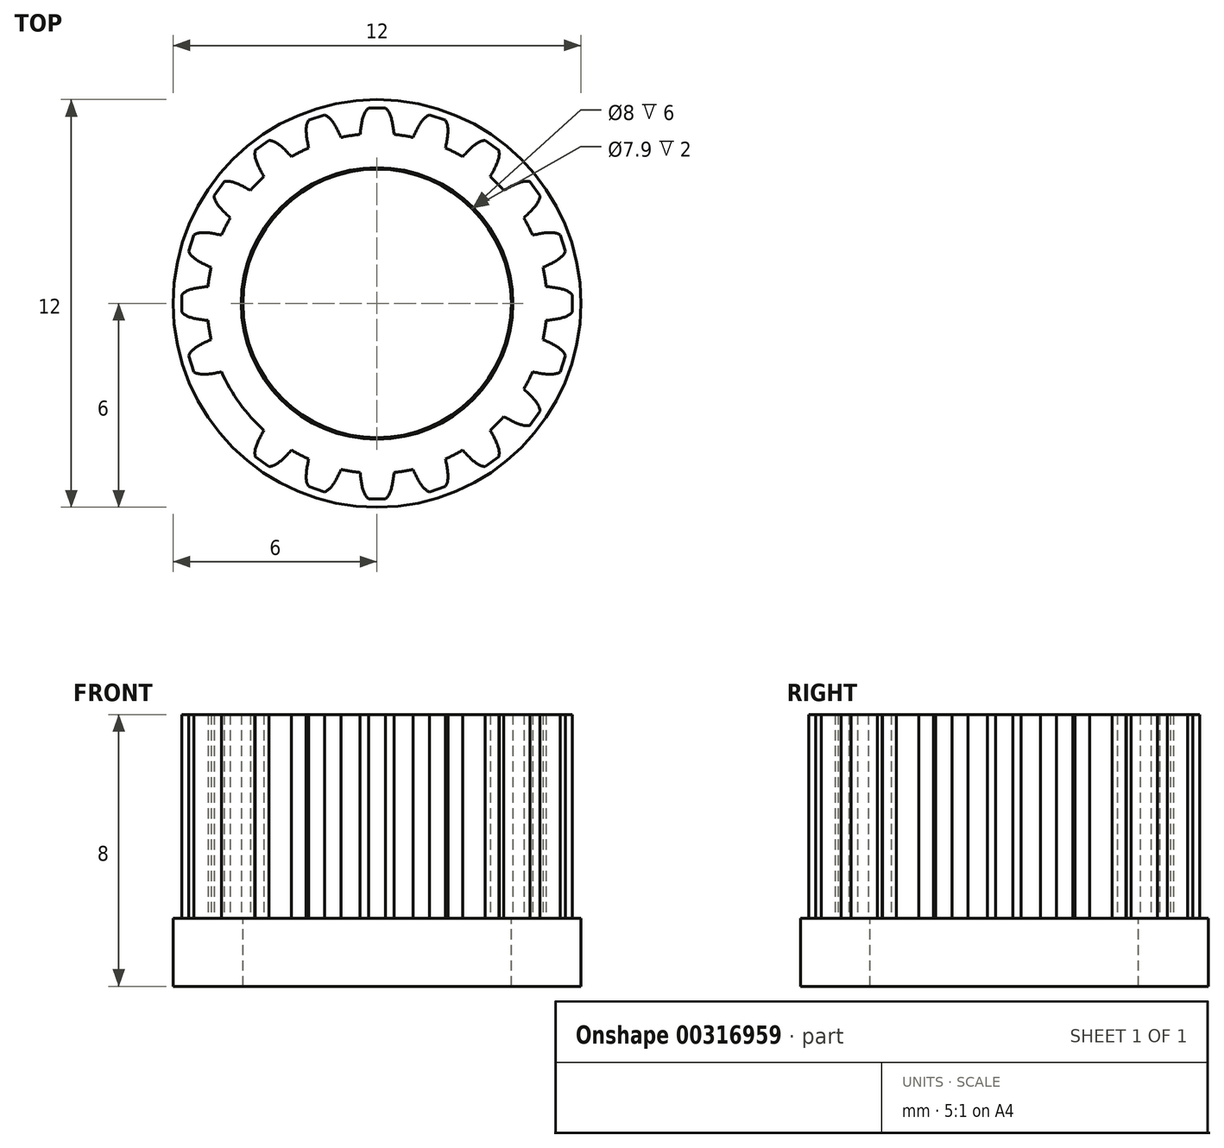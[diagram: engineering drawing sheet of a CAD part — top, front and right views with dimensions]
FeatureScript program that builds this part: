
annotation { "Feature Type Name" : "Feature", "Feature Type Description" : "" }
export const myFeature = defineFeature(function(context is Context, id is Id, definition is map)
    precondition{}
    {
        {
            var Q0;
            Q0=qCreatedBy(makeId("Top.planeOp"),FACE);
            var sketch = newSketch(context, id + "F0", { "sketchPlane" : qUnion([Q0])});
            skArc(sketch, "E0", {"start": v(-4, 0) * mm, "mid": v(-2.83, -2.83) * mm, "end": v(0, -4) * mm});
            skArc(sketch, "E1", {"start": v(0.5, -4.97) * mm, "mid": v(0, 5) * mm, "end": v(-0.5, -4.97) * mm});
            skPoint(sketch, "E2", {"position": v(0, -5) * mm});
            skPoint(sketch, "E3", {"position": v(-0.5, -4.97) * mm});
            skPoint(sketch, "E4", {"position": v(0.5, -4.97) * mm});
            skPoint(sketch, "E5.start.orphan", {"position": v(0, -5.75) * mm});
            skArc(sketch, "E6.1.0", {"start": v(2.01, -4.58) * mm, "mid": v(-1.55, 4.76) * mm, "end": v(1.06, -4.89) * mm});
            skArc(sketch, "E6.2.0", {"start": v(3.33, -3.73) * mm, "mid": v(-2.94, 4.05) * mm, "end": v(2.52, -4.32) * mm});
            skArc(sketch, "E6.3.0", {"start": v(4.32, -2.52) * mm, "mid": v(-4.05, 2.94) * mm, "end": v(3.73, -3.33) * mm});
            skArc(sketch, "E6.4.0", {"start": v(4.89, -1.06) * mm, "mid": v(-4.76, 1.55) * mm, "end": v(4.58, -2.01) * mm});
            skArc(sketch, "E6.5.0", {"start": v(4.97, 0.5) * mm, "mid": v(-5, 0) * mm, "end": v(4.97, -0.5) * mm});
            skArc(sketch, "E6.6.0", {"start": v(4.58, 2.01) * mm, "mid": v(-4.76, -1.55) * mm, "end": v(4.89, 1.06) * mm});
            skArc(sketch, "E6.7.0", {"start": v(3.73, 3.33) * mm, "mid": v(0.78, 4.94) * mm, "end": v(-2.52, 4.32) * mm});
            skArc(sketch, "E6.8.0", {"start": v(2.52, 4.32) * mm, "mid": v(-1.78, 4.67) * mm, "end": v(-4.76, 1.55) * mm});
            skArc(sketch, "E6.9.0", {"start": v(1.06, 4.89) * mm, "mid": v(-0.78, 4.94) * mm, "end": v(-2.52, 4.32) * mm});
            skArc(sketch, "E6.10.0", {"start": v(-0.5, 4.97) * mm, "mid": v(0, -5) * mm, "end": v(0.5, 4.97) * mm});
            skArc(sketch, "E6.11.0", {"start": v(-2.01, 4.58) * mm, "mid": v(-2.5, 4.34) * mm, "end": v(-2.94, 4.05) * mm});
            skArc(sketch, "E6.12.0", {"start": v(-3.33, 3.73) * mm, "mid": v(2.94, -4.05) * mm, "end": v(-2.52, 4.32) * mm});
            skArc(sketch, "E6.13.0", {"start": v(-4.32, 2.52) * mm, "mid": v(3.87, -3.16) * mm, "end": v(-3.33, 3.73) * mm});
            skArc(sketch, "E6.14.0", {"start": v(-4.89, 1.06) * mm, "mid": v(4.76, -1.55) * mm, "end": v(-4.58, 2.01) * mm});
            skArc(sketch, "E6.15.0", {"start": v(-4.97, -0.5) * mm, "mid": v(5, 0) * mm, "end": v(-4.97, 0.5) * mm});
            skArc(sketch, "E6.16.0", {"start": v(-4.58, -2.01) * mm, "mid": v(-2.04, -4.56) * mm, "end": v(1.55, -4.76) * mm});
            skArc(sketch, "E6.17.0", {"start": v(-3.73, -3.33) * mm, "mid": v(4.94, -0.78) * mm, "end": v(-2.52, 4.32) * mm});
            skArc(sketch, "E6.18.0", {"start": v(-2.52, -4.32) * mm, "mid": v(-1.3, -4.83) * mm, "end": v(0, -5) * mm});
            skArc(sketch, "E6.19.0", {"start": v(-1.06, -4.89) * mm, "mid": v(0, -5) * mm, "end": v(1.06, -4.89) * mm});
            skLineSegment(sketch, "E7", {"start": v(-1.78, -5.47) * mm, "end": v(-1.54, -5.55) * mm});
            skLineSegment(sketch, "E8", {"start": v(-1.78, -5.47) * mm, "end": v(-2.01, -5.4) * mm});
            skFitSpline(sketch, "E9", {"points": [v(-2.01, -4.58) * mm, v(-2.01, -5.4) * mm, v(-1.54, -5.55) * mm, v(-1.06, -4.89) * mm], "startDerivative": vector(-0.53, -2.62) * mm, "endDerivative": vector(1.11, 2.43) * mm});
            skLineSegment(sketch, "E10", {"start": v(0, -5.75) * mm, "end": v(-0.25, -5.75) * mm});
            skFitSpline(sketch, "E11", {"points": [v(-0.5, -4.97) * mm, v(-0.25, -5.75) * mm, v(0.25, -5.75) * mm, v(0.5, -4.97) * mm], "startDerivative": vector(0.3, -2.65) * mm, "endDerivative": vector(0.3, 2.65) * mm});
            skLineSegment(sketch, "E12", {"start": v(-3.38, -4.65) * mm, "end": v(-3.18, -4.8) * mm});
            skLineSegment(sketch, "E13", {"start": v(-3.38, -4.65) * mm, "end": v(-3.58, -4.5) * mm});
            skFitSpline(sketch, "E14", {"points": [v(-3.33, -3.73) * mm, v(-3.58, -4.5) * mm, v(-3.18, -4.8) * mm, v(-2.52, -4.32) * mm], "startDerivative": vector(-1.31, -2.33) * mm, "endDerivative": vector(1.8, 1.97) * mm});
            skPoint(sketch, "E15.orphan", {"position": v(-2.94, -4.05) * mm});
            skLineSegment(sketch, "E16", {"start": v(-4.65, -3.38) * mm, "end": v(-4.5, -3.58) * mm});
            skLineSegment(sketch, "E17", {"start": v(-4.5, -3.58) * mm, "end": v(-4.65, -3.38) * mm});
            skLineSegment(sketch, "E18", {"start": v(-4.65, -3.38) * mm, "end": v(-4.8, -3.18) * mm});
            skFitSpline(sketch, "E19", {"points": [v(-4.32, -2.52) * mm, v(-4.8, -3.18) * mm, v(-4.5, -3.58) * mm, v(-3.73, -3.33) * mm], "startDerivative": vector(-1.97, -1.8) * mm, "endDerivative": vector(2.33, 1.31) * mm});
            skPoint(sketch, "E20.orphan", {"position": v(-4.05, -2.94) * mm});
            skLineSegment(sketch, "E21", {"start": v(-5.47, -1.78) * mm, "end": v(-5.4, -2.01) * mm});
            skLineSegment(sketch, "E22", {"start": v(-5.47, -1.78) * mm, "end": v(-5.55, -1.54) * mm});
            skFitSpline(sketch, "E23", {"points": [v(-4.89, -1.06) * mm, v(-5.55, -1.54) * mm, v(-5.4, -2.01) * mm, v(-4.58, -2.01) * mm], "startDerivative": vector(-2.43, -1.11) * mm, "endDerivative": vector(2.62, 0.53) * mm});
            skPoint(sketch, "E24.orphan", {"position": v(-4.76, -1.55) * mm});
            skLineSegment(sketch, "E25", {"start": v(-5.75, 0) * mm, "end": v(-5.75, -0.25) * mm});
            skFitSpline(sketch, "E26.trimOffspring", {"points": [v(-4.97, 0.5) * mm, v(-5.75, 0.25) * mm, v(-5.75, -0.25) * mm, v(-4.97, -0.5) * mm], "startDerivative": vector(-2.65, -0.3) * mm, "endDerivative": vector(2.65, -0.3) * mm});
            skPoint(sketch, "E27.orphan", {"position": v(-5, 0) * mm});
            skArc(sketch, "E28.trimOffspring", {"start": v(-5, 0) * mm, "mid": v(-4.19, -2.73) * mm, "end": v(-2.01, -4.58) * mm});
            skArc(sketch, "E29.trimOffspring", {"start": v(-5, 0) * mm, "mid": v(-4.56, -2.04) * mm, "end": v(-3.33, -3.73) * mm});
            skPoint(sketch, "E30.start.orphan", {"position": v(-4.76, 1.55) * mm});
            skPoint(sketch, "E31.start.orphan", {"position": v(-2.94, 4.05) * mm});
            skArc(sketch, "E32.trimOffspring", {"start": v(-2.94, 4.05) * mm, "mid": v(-4.9, 1.03) * mm, "end": v(-4.32, -2.52) * mm});
            skArc(sketch, "E33.trimOffspring", {"start": v(-3.33, 3.73) * mm, "mid": v(-4.46, 2.27) * mm, "end": v(-4.97, 0.5) * mm});
            skPoint(sketch, "E34.orphan", {"position": v(-3.73, 3.33) * mm});
            skPoint(sketch, "E35.start.orphan", {"position": v(-4.05, 2.94) * mm});
            skPoint(sketch, "E36.start.orphan", {"position": v(-1.55, 4.76) * mm});
            skPoint(sketch, "E37.start.orphan", {"position": v(0, 5) * mm});
            skPoint(sketch, "E38.start.orphan", {"position": v(2.94, -4.05) * mm});
            skPoint(sketch, "E39.start.orphan", {"position": v(1.55, -4.76) * mm});
            skArc(sketch, "E40.trimOffspring", {"start": v(0.5, -4.97) * mm, "mid": v(4.76, -1.55) * mm, "end": v(3.33, 3.73) * mm});
            skArc(sketch, "E41.trimOffspring", {"start": v(1.55, -4.76) * mm, "mid": v(2.27, -4.46) * mm, "end": v(2.94, -4.05) * mm});
            skArc(sketch, "E42.trimOffspring", {"start": v(2.01, -4.58) * mm, "mid": v(2.7, -4.2) * mm, "end": v(3.33, -3.73) * mm});
            skArc(sketch, "E43.trimOffspring", {"start": v(3.33, -3.73) * mm, "mid": v(4.94, -0.78) * mm, "end": v(4.32, 2.52) * mm});
            skArc(sketch, "E44.trimOffspring", {"start": v(3.33, -3.73) * mm, "mid": v(3.54, -3.54) * mm, "end": v(3.73, -3.33) * mm});
            skArc(sketch, "E45.trimOffspring", {"start": v(3.73, -3.33) * mm, "mid": v(3.87, 3.16) * mm, "end": v(-2.52, 4.32) * mm});
            skArc(sketch, "E46.trimOffspring", {"start": v(4.32, -2.52) * mm, "mid": v(4.94, 0.78) * mm, "end": v(3.33, 3.73) * mm});
            skPoint(sketch, "E47.start.orphan", {"position": v(4.76, -1.55) * mm});
            skPoint(sketch, "E48.start.orphan", {"position": v(5, 0) * mm});
            skArc(sketch, "E49.trimOffspring", {"start": v(2.52, 4.32) * mm, "mid": v(-0.25, 5) * mm, "end": v(-2.94, 4.05) * mm});
            skArc(sketch, "E50.trimOffspring", {"start": v(2.52, 4.32) * mm, "mid": v(-1.55, 4.76) * mm, "end": v(-4.58, 2.01) * mm});
            skArc(sketch, "E51.trimOffspring", {"start": v(3.73, 3.33) * mm, "mid": v(3.54, 3.54) * mm, "end": v(3.33, 3.73) * mm});
            skArc(sketch, "E52.trimOffspring", {"start": v(-4.76, 1.55) * mm, "mid": v(-4.83, 1.3) * mm, "end": v(-4.89, 1.06) * mm});
            skArc(sketch, "E53.trimOffspring", {"start": v(-4.89, 1.06) * mm, "mid": v(-2.73, -4.19) * mm, "end": v(2.94, -4.05) * mm});
            skFitSpline(sketch, "E54.MirrorCS", {"points": [v(-4.97, -0.5) * mm, v(-5.75, -0.25) * mm, v(-5.75, 0.25) * mm, v(-4.97, 0.5) * mm], "startDerivative": vector(-2.65, 0.3) * mm, "endDerivative": vector(2.65, 0.3) * mm});
            skFitSpline(sketch, "E55.MirrorCS", {"points": [v(-4.89, 1.06) * mm, v(-5.55, 1.54) * mm, v(-5.4, 2.01) * mm, v(-4.58, 2.01) * mm], "startDerivative": vector(-2.43, 1.11) * mm, "endDerivative": vector(2.62, -0.53) * mm});
            skLineSegment(sketch, "E56.MirrorCS", {"start": v(-5.47, 1.78) * mm, "end": v(-5.4, 2.01) * mm});
            skLineSegment(sketch, "E57.MirrorCS", {"start": v(-5.47, 1.78) * mm, "end": v(-5.55, 1.54) * mm});
            skLineSegment(sketch, "E58.MirrorCS", {"start": v(-5.75, 0) * mm, "end": v(-5.75, 0.25) * mm});
            skFitSpline(sketch, "E59.MirrorCS", {"points": [v(-4.32, 2.52) * mm, v(-4.8, 3.18) * mm, v(-4.5, 3.58) * mm, v(-3.73, 3.33) * mm], "startDerivative": vector(-1.97, 1.8) * mm, "endDerivative": vector(2.33, -1.31) * mm});
            skLineSegment(sketch, "E60.MirrorCS", {"start": v(-4.5, 3.58) * mm, "end": v(-4.65, 3.38) * mm});
            skLineSegment(sketch, "E61.MirrorCS", {"start": v(-4.65, 3.38) * mm, "end": v(-4.8, 3.18) * mm});
            skFitSpline(sketch, "E62.MirrorCS", {"points": [v(-4.32, 2.52) * mm, v(-4.8, 3.18) * mm, v(-4.5, 3.58) * mm, v(-3.73, 3.33) * mm], "startDerivative": vector(-1.97, 1.8) * mm, "endDerivative": vector(2.33, -1.31) * mm});
            skFitSpline(sketch, "E63.MirrorCS", {"points": [v(-3.33, 3.73) * mm, v(-3.58, 4.5) * mm, v(-3.18, 4.8) * mm, v(-2.52, 4.32) * mm], "startDerivative": vector(-1.31, 2.33) * mm, "endDerivative": vector(1.8, -1.97) * mm});
            skLineSegment(sketch, "E64.MirrorCS", {"start": v(-3.38, 4.65) * mm, "end": v(-3.58, 4.5) * mm});
            skLineSegment(sketch, "E65.MirrorCS", {"start": v(-3.38, 4.65) * mm, "end": v(-3.18, 4.8) * mm});
            skFitSpline(sketch, "E66.MirrorCS", {"points": [v(-3.33, 3.73) * mm, v(-3.58, 4.5) * mm, v(-3.18, 4.8) * mm, v(-2.52, 4.32) * mm], "startDerivative": vector(-1.31, 2.33) * mm, "endDerivative": vector(1.8, -1.97) * mm});
            skArc(sketch, "E67.MirrorCS", {"start": v(-4, 0) * mm, "mid": v(-2.83, 2.83) * mm, "end": v(0, 4) * mm});
            skLineSegment(sketch, "E68.MirrorCS", {"start": v(0, 5.75) * mm, "end": v(-0.25, 5.75) * mm});
            skFitSpline(sketch, "E69.MirrorCS", {"points": [v(-0.5, 4.97) * mm, v(-0.25, 5.75) * mm, v(0.25, 5.75) * mm, v(0.5, 4.97) * mm], "startDerivative": vector(0.3, 2.65) * mm, "endDerivative": vector(0.3, -2.65) * mm});
            skFitSpline(sketch, "E70.MirrorCS", {"points": [v(-2.01, 4.58) * mm, v(-2.01, 5.4) * mm, v(-1.54, 5.55) * mm, v(-1.06, 4.89) * mm], "startDerivative": vector(-0.53, 2.62) * mm, "endDerivative": vector(1.11, -2.43) * mm});
            skLineSegment(sketch, "E71.MirrorCS", {"start": v(-1.78, 5.47) * mm, "end": v(-1.54, 5.55) * mm});
            skLineSegment(sketch, "E72.MirrorCS", {"start": v(-1.78, 5.47) * mm, "end": v(-2.01, 5.4) * mm});
            skArc(sketch, "E73.trimOffspring", {"start": v(-2.94, 4.05) * mm, "mid": v(0.53, -4.97) * mm, "end": v(2.01, 4.58) * mm});
            skArc(sketch, "E74.trimOffspring", {"start": v(-3.33, 3.73) * mm, "mid": v(2.27, -4.46) * mm, "end": v(-1.06, 4.89) * mm});
            skArc(sketch, "E75.trimOffspring", {"start": v(-2.94, 4.05) * mm, "mid": v(-1.03, -4.9) * mm, "end": v(4.32, 2.52) * mm});
            skArc(sketch, "E76.trimOffspring", {"start": v(-2.94, 4.05) * mm, "mid": v(-4.67, 1.78) * mm, "end": v(-4.89, -1.06) * mm});
            skArc(sketch, "E77.MirrorCS", {"start": v(4, 0) * mm, "mid": v(2.83, 2.83) * mm, "end": v(0, 4) * mm});
            skFitSpline(sketch, "E78.MirrorCS", {"points": [v(0.5, 4.97) * mm, v(0.25, 5.75) * mm, v(-0.25, 5.75) * mm, v(-0.5, 4.97) * mm], "startDerivative": vector(-0.3, 2.65) * mm, "endDerivative": vector(-0.3, -2.65) * mm});
            skLineSegment(sketch, "E79.MirrorCS", {"start": v(0, 5.75) * mm, "end": v(0.25, 5.75) * mm});
            skFitSpline(sketch, "E80.MirrorCS", {"points": [v(2.01, 4.58) * mm, v(2.01, 5.4) * mm, v(1.54, 5.55) * mm, v(1.06, 4.89) * mm], "startDerivative": vector(0.53, 2.62) * mm, "endDerivative": vector(-1.11, -2.43) * mm});
            skLineSegment(sketch, "E81.MirrorCS", {"start": v(1.78, 5.47) * mm, "end": v(2.01, 5.4) * mm});
            skLineSegment(sketch, "E82.MirrorCS", {"start": v(1.78, 5.47) * mm, "end": v(1.54, 5.55) * mm});
            skFitSpline(sketch, "E83.MirrorCS", {"points": [v(3.33, 3.73) * mm, v(3.58, 4.5) * mm, v(3.18, 4.8) * mm, v(2.52, 4.32) * mm], "startDerivative": vector(1.31, 2.33) * mm, "endDerivative": vector(-1.8, -1.97) * mm});
            skLineSegment(sketch, "E84.MirrorCS", {"start": v(3.38, 4.65) * mm, "end": v(3.18, 4.8) * mm});
            skLineSegment(sketch, "E85.MirrorCS", {"start": v(3.38, 4.65) * mm, "end": v(3.58, 4.5) * mm});
            skFitSpline(sketch, "E86.MirrorCS", {"points": [v(3.33, 3.73) * mm, v(3.58, 4.5) * mm, v(3.18, 4.8) * mm, v(2.52, 4.32) * mm], "startDerivative": vector(1.31, 2.33) * mm, "endDerivative": vector(-1.8, -1.97) * mm});
            skFitSpline(sketch, "E87.MirrorCS", {"points": [v(4.32, 2.52) * mm, v(4.8, 3.18) * mm, v(4.5, 3.58) * mm, v(3.73, 3.33) * mm], "startDerivative": vector(1.97, 1.8) * mm, "endDerivative": vector(-2.33, -1.31) * mm});
            skLineSegment(sketch, "E88.MirrorCS", {"start": v(4.5, 3.58) * mm, "end": v(4.65, 3.38) * mm});
            skLineSegment(sketch, "E89.MirrorCS", {"start": v(4.65, 3.38) * mm, "end": v(4.8, 3.18) * mm});
            skFitSpline(sketch, "E90.MirrorCS", {"points": [v(4.32, 2.52) * mm, v(4.8, 3.18) * mm, v(4.5, 3.58) * mm, v(3.73, 3.33) * mm], "startDerivative": vector(1.97, 1.8) * mm, "endDerivative": vector(-2.33, -1.31) * mm});
            skFitSpline(sketch, "E91.MirrorCS", {"points": [v(4.89, 1.06) * mm, v(5.55, 1.54) * mm, v(5.4, 2.01) * mm, v(4.58, 2.01) * mm], "startDerivative": vector(2.43, 1.11) * mm, "endDerivative": vector(-2.62, -0.53) * mm});
            skLineSegment(sketch, "E92.MirrorCS", {"start": v(5.47, 1.78) * mm, "end": v(5.55, 1.54) * mm});
            skLineSegment(sketch, "E93.MirrorCS", {"start": v(5.47, 1.78) * mm, "end": v(5.4, 2.01) * mm});
            skFitSpline(sketch, "E94.MirrorCS", {"points": [v(4.97, -0.5) * mm, v(5.75, -0.25) * mm, v(5.75, 0.25) * mm, v(4.97, 0.5) * mm], "startDerivative": vector(2.65, 0.3) * mm, "endDerivative": vector(-2.65, 0.3) * mm});
            skLineSegment(sketch, "E95.MirrorCS", {"start": v(5.75, 0) * mm, "end": v(5.75, 0.25) * mm});
            skArc(sketch, "E96.MirrorCS", {"start": v(4, 0) * mm, "mid": v(2.83, -2.83) * mm, "end": v(0, -4) * mm});
            skLineSegment(sketch, "E97.MirrorCS", {"start": v(0, -5.75) * mm, "end": v(0.25, -5.75) * mm});
            skFitSpline(sketch, "E98.MirrorCS", {"points": [v(0.5, -4.97) * mm, v(0.25, -5.75) * mm, v(-0.25, -5.75) * mm, v(-0.5, -4.97) * mm], "startDerivative": vector(-0.3, -2.65) * mm, "endDerivative": vector(-0.3, 2.65) * mm});
            skFitSpline(sketch, "E99.MirrorCS", {"points": [v(2.01, -4.58) * mm, v(2.01, -5.4) * mm, v(1.54, -5.55) * mm, v(1.06, -4.89) * mm], "startDerivative": vector(0.53, -2.62) * mm, "endDerivative": vector(-1.11, 2.43) * mm});
            skLineSegment(sketch, "E100.MirrorCS", {"start": v(1.78, -5.47) * mm, "end": v(1.54, -5.55) * mm});
            skLineSegment(sketch, "E101.MirrorCS", {"start": v(1.78, -5.47) * mm, "end": v(2.01, -5.4) * mm});
            skFitSpline(sketch, "E102.MirrorCS", {"points": [v(3.33, -3.73) * mm, v(3.58, -4.5) * mm, v(3.18, -4.8) * mm, v(2.52, -4.32) * mm], "startDerivative": vector(1.31, -2.33) * mm, "endDerivative": vector(-1.8, 1.97) * mm});
            skLineSegment(sketch, "E103.MirrorCS", {"start": v(3.38, -4.65) * mm, "end": v(3.18, -4.8) * mm});
            skLineSegment(sketch, "E104.MirrorCS", {"start": v(3.38, -4.65) * mm, "end": v(3.58, -4.5) * mm});
            skFitSpline(sketch, "E105.MirrorCS", {"points": [v(4.32, -2.52) * mm, v(4.8, -3.18) * mm, v(4.5, -3.58) * mm, v(3.73, -3.33) * mm], "startDerivative": vector(1.97, -1.8) * mm, "endDerivative": vector(-2.33, 1.31) * mm});
            skLineSegment(sketch, "E106.MirrorCS", {"start": v(4.5, -3.58) * mm, "end": v(4.65, -3.38) * mm});
            skLineSegment(sketch, "E107.MirrorCS", {"start": v(4.65, -3.38) * mm, "end": v(4.8, -3.18) * mm});
            skFitSpline(sketch, "E108.MirrorCS", {"points": [v(4.89, -1.06) * mm, v(5.55, -1.54) * mm, v(5.4, -2.01) * mm, v(4.58, -2.01) * mm], "startDerivative": vector(2.43, -1.11) * mm, "endDerivative": vector(-2.62, 0.53) * mm});
            skLineSegment(sketch, "E109.MirrorCS", {"start": v(5.47, -1.78) * mm, "end": v(5.4, -2.01) * mm});
            skLineSegment(sketch, "E110.MirrorCS", {"start": v(5.47, -1.78) * mm, "end": v(5.55, -1.54) * mm});
            skFitSpline(sketch, "E111.MirrorCS", {"points": [v(4.97, 0.5) * mm, v(5.75, 0.25) * mm, v(5.75, -0.25) * mm, v(4.97, -0.5) * mm], "startDerivative": vector(2.65, -0.3) * mm, "endDerivative": vector(-2.65, -0.3) * mm});
            skLineSegment(sketch, "E112.MirrorCS", {"start": v(5.75, 0) * mm, "end": v(5.75, -0.25) * mm});
            skFitSpline(sketch, "E113.MirrorCS", {"points": [v(3.33, -3.73) * mm, v(3.58, -4.5) * mm, v(3.18, -4.8) * mm, v(2.52, -4.32) * mm], "startDerivative": vector(1.31, -2.33) * mm, "endDerivative": vector(-1.8, 1.97) * mm});
            skFitSpline(sketch, "E114.MirrorCS", {"points": [v(4.32, -2.52) * mm, v(4.8, -3.18) * mm, v(4.5, -3.58) * mm, v(3.73, -3.33) * mm], "startDerivative": vector(1.97, -1.8) * mm, "endDerivative": vector(-2.33, 1.31) * mm});
            skSolve(sketch);
        }
        {
            var Q0;
            {var subQ0=sQuery(id+"F0.wireOp",EDGE,"E70.MirrorCS");Q0=makeQuery(id+"F0.imprint","IMPRINT",FACE,{"disambiguationData":[TD([[makeQuery(id+"F0.imprint","IMPRINT",EDGE,{"derivedFrom":subQ0}),-1.0]])]});}
            var Q1;
            {var subQ0=sQuery(id+"F0.wireOp",EDGE,"E63.MirrorCS");Q1=makeQuery(id+"F0.imprint","IMPRINT",FACE,{"disambiguationData":[TD([[makeQuery(id+"F0.imprint","IMPRINT",EDGE,{"derivedFrom":subQ0}),-1.0]])]});}
            var Q2;
            {var subQ1=sQuery(id+"F0.wireOp",EDGE,"E59.MirrorCS");Q2=makeQuery(id+"F0.imprint","IMPRINT",FACE,{"disambiguationData":[TD([[makeQuery(id+"F0.imprint","IMPRINT",EDGE,{"derivedFrom":subQ1}),-1.0]])]});}
            var Q3;
            {var subQ2=sQuery(id+"F0.wireOp",EDGE,"E55.MirrorCS");Q3=makeQuery(id+"F0.imprint","IMPRINT",FACE,{"disambiguationData":[TD([[makeQuery(id+"F0.imprint","IMPRINT",EDGE,{"derivedFrom":subQ2}),-1.0]])]});}
            var Q4;
            Q4=makeQuery(id+"F0.imprint","IMPRINT",FACE,{"disambiguationData":[TD([[makeQuery(id+"F0.imprint","IMPRINT",EDGE,{"derivedFrom":sQuery(id+"F0.wireOp",EDGE,"E25")}),1.0]])]});
            var Q5;
            Q5=makeQuery(id+"F0.imprint","IMPRINT",FACE,{"disambiguationData":[TD([[makeQuery(id+"F0.imprint","IMPRINT",EDGE,{"derivedFrom":sQuery(id+"F0.wireOp",EDGE,"E21")}),1.0]])]});
            var Q6;
            Q6=makeQuery(id+"F0.imprint","IMPRINT",FACE,{"disambiguationData":[TD([[makeQuery(id+"F0.imprint","IMPRINT",EDGE,{"derivedFrom":sQuery(id+"F0.wireOp",EDGE,"E17")}),-1.0]])]});
            var Q7;
            Q7=makeQuery(id+"F0.imprint","IMPRINT",FACE,{"disambiguationData":[TD([[makeQuery(id+"F0.imprint","IMPRINT",EDGE,{"derivedFrom":sQuery(id+"F0.wireOp",EDGE,"E12")}),1.0]])]});
            var Q8;
            Q8=makeQuery(id+"F0.imprint","IMPRINT",FACE,{"disambiguationData":[TD([[makeQuery(id+"F0.imprint","IMPRINT",EDGE,{"derivedFrom":sQuery(id+"F0.wireOp",EDGE,"E7")}),1.0]])]});
            var Q9;
            {var subQ0=sQuery(id+"F0.wireOp",EDGE,"E99.MirrorCS");Q9=makeQuery(id+"F0.imprint","IMPRINT",FACE,{"disambiguationData":[TD([[makeQuery(id+"F0.imprint","IMPRINT",EDGE,{"derivedFrom":subQ0}),-1.0]])]});}
            var Q10;
            Q10=makeQuery(id+"F0.imprint","IMPRINT",FACE,{"disambiguationData":[TD([[makeQuery(id+"F0.imprint","IMPRINT",EDGE,{"derivedFrom":sQuery(id+"F0.wireOp",EDGE,"E10")}),-1.0]])]});
            var Q11;
            {var subQ0=sQuery(id+"F0.wireOp",EDGE,"E102.MirrorCS");Q11=makeQuery(id+"F0.imprint","IMPRINT",FACE,{"disambiguationData":[TD([[makeQuery(id+"F0.imprint","IMPRINT",EDGE,{"derivedFrom":subQ0}),-1.0]])]});}
            var Q12;
            Q12=makeQuery(id+"F0.imprint","IMPRINT",FACE,{"disambiguationData":[TD([[makeQuery(id+"F0.imprint","IMPRINT",EDGE,{"derivedFrom":sQuery(id+"F0.wireOp",EDGE,"E106.MirrorCS")}),1.0]])]});
            var Q13;
            {var subQ0=sQuery(id+"F0.wireOp",EDGE,"E108.MirrorCS");Q13=makeQuery(id+"F0.imprint","IMPRINT",FACE,{"disambiguationData":[TD([[makeQuery(id+"F0.imprint","IMPRINT",EDGE,{"derivedFrom":subQ0}),-1.0]])]});}
            var Q14;
            {var subQ1=sQuery(id+"F0.wireOp",EDGE,"E94.MirrorCS");Q14=makeQuery(id+"F0.imprint","IMPRINT",FACE,{"disambiguationData":[TD([[makeQuery(id+"F0.imprint","IMPRINT",EDGE,{"derivedFrom":subQ1}),1.0]])]});}
            var Q15;
            {var subQ0=sQuery(id+"F0.wireOp",EDGE,"E91.MirrorCS");Q15=makeQuery(id+"F0.imprint","IMPRINT",FACE,{"disambiguationData":[TD([[makeQuery(id+"F0.imprint","IMPRINT",EDGE,{"derivedFrom":subQ0}),1.0]])]});}
            var Q16;
            {var subQ1=sQuery(id+"F0.wireOp",EDGE,"E80.MirrorCS");Q16=makeQuery(id+"F0.imprint","IMPRINT",FACE,{"disambiguationData":[TD([[makeQuery(id+"F0.imprint","IMPRINT",EDGE,{"derivedFrom":subQ1}),1.0]])]});}
            var Q17;
            Q17=makeQuery(id+"F0.imprint","IMPRINT",FACE,{"disambiguationData":[TD([[makeQuery(id+"F0.imprint","IMPRINT",EDGE,{"derivedFrom":sQuery(id+"F0.wireOp",EDGE,"E85.MirrorCS")}),-1.0]])]});
            var Q18;
            Q18=makeQuery(id+"F0.imprint","IMPRINT",FACE,{"disambiguationData":[TD([[makeQuery(id+"F0.imprint","IMPRINT",EDGE,{"derivedFrom":sQuery(id+"F0.wireOp",EDGE,"E68.MirrorCS")}),1.0]])]});
            var Q19;
            {var subQ0=sQuery(id+"F0.wireOp",EDGE,"E87.MirrorCS");Q19=makeQuery(id+"F0.imprint","IMPRINT",FACE,{"disambiguationData":[TD([[makeQuery(id+"F0.imprint","IMPRINT",EDGE,{"derivedFrom":subQ0}),1.0]])]});}
            var Q20;
            Q20=makeQuery(id+"F0.imprint","IMPRINT",FACE,{"disambiguationData":[TD([[makeQuery(id+"F0.imprint","IMPRINT",EDGE,{"derivedFrom":sQuery(id+"F0.wireOp",EDGE,"E0")}),-1.0]])]});
            extrude(context, id + "F1", {"entities" : qUnion([Q0, Q1, Q2, Q3, Q4, Q5, Q6, Q7, Q8, Q9, Q10, Q11, Q12, Q13, Q14, Q15, Q16, Q17, Q18, Q19, Q20]), "depth" : 6 * mm});
        }
        {
            var Q0;
            Q0=qCreatedBy(makeId("Top.planeOp"),FACE);
            var sketch = newSketch(context, id + "F2", { "sketchPlane" : qUnion([Q0])});
            skCircle(sketch, "E115", {"center": v(0, 0) * mm, "radius": 6 * mm});
            skSolve(sketch);
        }
        {
            var Q0;
            Q0=makeQuery(id+"F2.imprint","IMPRINT",FACE,{"disambiguationData":[TD([[makeQuery(id+"F2.imprint","IMPRINT",EDGE,{"derivedFrom":sQuery(id+"F2.wireOp",EDGE,"E115")}),1.0]])]});
            extrude(context, id + "F3", {"entities" : qUnion([Q0]), "operationType" : NewBodyOperationType.ADD, "oppositeDirection" : true, "depth" : 2 * mm});
        }
        {
            var Q0;
            Q0=sQuery(id+"F2.wireOp",VERTEX,"E115.center");
            var Q1;
            Q1=makeQuery(id+"F1.opExtrude","SWEPT_BODY",BODY,{"disambiguationData":[OSD([sQuery(id+"F0.wireOp",EDGE,"E0"),sQuery(id+"F0.wireOp",EDGE,"E7"),sQuery(id+"F0.wireOp",EDGE,"E8"),sQuery(id+"F0.wireOp",EDGE,"E9"),sQuery(id+"F0.wireOp",EDGE,"E9"),sQuery(id+"F0.wireOp",EDGE,"E10"),sQuery(id+"F0.wireOp",EDGE,"E11"),sQuery(id+"F0.wireOp",EDGE,"E12"),sQuery(id+"F0.wireOp",EDGE,"E13"),sQuery(id+"F0.wireOp",EDGE,"E14"),sQuery(id+"F0.wireOp",EDGE,"E14"),sQuery(id+"F0.wireOp",EDGE,"E17"),sQuery(id+"F0.wireOp",EDGE,"E18"),sQuery(id+"F0.wireOp",EDGE,"E19"),sQuery(id+"F0.wireOp",EDGE,"E19"),sQuery(id+"F0.wireOp",EDGE,"E21"),sQuery(id+"F0.wireOp",EDGE,"E22"),sQuery(id+"F0.wireOp",EDGE,"E23"),sQuery(id+"F0.wireOp",EDGE,"E23"),sQuery(id+"F0.wireOp",EDGE,"E25"),sQuery(id+"F0.wireOp",EDGE,"E26.trimOffspring"),sQuery(id+"F0.wireOp",EDGE,"E50.trimOffspring"),sQuery(id+"F0.wireOp",EDGE,"E54.MirrorCS"),sQuery(id+"F0.wireOp",EDGE,"E55.MirrorCS"),sQuery(id+"F0.wireOp",EDGE,"E56.MirrorCS"),sQuery(id+"F0.wireOp",EDGE,"E57.MirrorCS"),sQuery(id+"F0.wireOp",EDGE,"E55.MirrorCS"),sQuery(id+"F0.wireOp",EDGE,"E58.MirrorCS"),sQuery(id+"F0.wireOp",EDGE,"E59.MirrorCS"),sQuery(id+"F0.wireOp",EDGE,"E60.MirrorCS"),sQuery(id+"F0.wireOp",EDGE,"E61.MirrorCS"),sQuery(id+"F0.wireOp",EDGE,"E62.MirrorCS"),sQuery(id+"F0.wireOp",EDGE,"E63.MirrorCS"),sQuery(id+"F0.wireOp",EDGE,"E64.MirrorCS"),sQuery(id+"F0.wireOp",EDGE,"E65.MirrorCS"),sQuery(id+"F0.wireOp",EDGE,"E66.MirrorCS"),sQuery(id+"F0.wireOp",EDGE,"E67.MirrorCS"),sQuery(id+"F0.wireOp",EDGE,"E68.MirrorCS"),sQuery(id+"F0.wireOp",EDGE,"E69.MirrorCS"),sQuery(id+"F0.wireOp",EDGE,"E70.MirrorCS"),sQuery(id+"F0.wireOp",EDGE,"E71.MirrorCS"),sQuery(id+"F0.wireOp",EDGE,"E72.MirrorCS"),sQuery(id+"F0.wireOp",EDGE,"E70.MirrorCS"),sQuery(id+"F0.wireOp",EDGE,"E74.trimOffspring"),sQuery(id+"F0.wireOp",EDGE,"E75.trimOffspring"),sQuery(id+"F0.wireOp",EDGE,"E76.trimOffspring"),sQuery(id+"F0.wireOp",EDGE,"E77.MirrorCS"),sQuery(id+"F0.wireOp",EDGE,"E78.MirrorCS"),sQuery(id+"F0.wireOp",EDGE,"E79.MirrorCS"),sQuery(id+"F0.wireOp",EDGE,"E80.MirrorCS"),sQuery(id+"F0.wireOp",EDGE,"E80.MirrorCS"),sQuery(id+"F0.wireOp",EDGE,"E81.MirrorCS"),sQuery(id+"F0.wireOp",EDGE,"E82.MirrorCS"),sQuery(id+"F0.wireOp",EDGE,"E85.MirrorCS"),sQuery(id+"F0.wireOp",EDGE,"E84.MirrorCS"),sQuery(id+"F0.wireOp",EDGE,"E86.MirrorCS"),sQuery(id+"F0.wireOp",EDGE,"E87.MirrorCS"),sQuery(id+"F0.wireOp",EDGE,"E89.MirrorCS"),sQuery(id+"F0.wireOp",EDGE,"E88.MirrorCS"),sQuery(id+"F0.wireOp",EDGE,"E90.MirrorCS"),sQuery(id+"F0.wireOp",EDGE,"E91.MirrorCS"),sQuery(id+"F0.wireOp",EDGE,"E92.MirrorCS"),sQuery(id+"F0.wireOp",EDGE,"E93.MirrorCS"),sQuery(id+"F0.wireOp",EDGE,"E91.MirrorCS"),sQuery(id+"F0.wireOp",EDGE,"E94.MirrorCS"),sQuery(id+"F0.wireOp",EDGE,"E95.MirrorCS"),sQuery(id+"F0.wireOp",EDGE,"E96.MirrorCS"),sQuery(id+"F0.wireOp",EDGE,"E97.MirrorCS"),sQuery(id+"F0.wireOp",EDGE,"E98.MirrorCS"),sQuery(id+"F0.wireOp",EDGE,"E99.MirrorCS"),sQuery(id+"F0.wireOp",EDGE,"E100.MirrorCS"),sQuery(id+"F0.wireOp",EDGE,"E101.MirrorCS"),sQuery(id+"F0.wireOp",EDGE,"E99.MirrorCS"),sQuery(id+"F0.wireOp",EDGE,"E102.MirrorCS"),sQuery(id+"F0.wireOp",EDGE,"E103.MirrorCS"),sQuery(id+"F0.wireOp",EDGE,"E104.MirrorCS"),sQuery(id+"F0.wireOp",EDGE,"E106.MirrorCS"),sQuery(id+"F0.wireOp",EDGE,"E107.MirrorCS"),sQuery(id+"F0.wireOp",EDGE,"E108.MirrorCS"),sQuery(id+"F0.wireOp",EDGE,"E109.MirrorCS"),sQuery(id+"F0.wireOp",EDGE,"E110.MirrorCS"),sQuery(id+"F0.wireOp",EDGE,"E108.MirrorCS"),sQuery(id+"F0.wireOp",EDGE,"E111.MirrorCS"),sQuery(id+"F0.wireOp",EDGE,"E112.MirrorCS"),sQuery(id+"F0.wireOp",EDGE,"E105.MirrorCS"),sQuery(id+"F0.wireOp",EDGE,"E83.MirrorCS"),sQuery(id+"F0.wireOp",EDGE,"E114.MirrorCS"),sQuery(id+"F0.wireOp",EDGE,"E113.MirrorCS")])]});
            hole(context, id + "F4", {"style" : HoleStyle.SIMPLE, "endStyle" : HoleEndStyle.THROUGH, "holeDiameter" : 7.9 * mm, "tappedDepth" : 12 * mm, "tapClearance" : 3, "locations" : qUnion([Q0]), "scope" : qUnion([Q1])});
        }
        {
            var Q0;
            Q0=qCreatedBy(makeId("Top.planeOp"),FACE);
            var sketch = newSketch(context, id + "F5", { "sketchPlane" : qUnion([Q0])});
            skCircle(sketch, "E116", {"center": v(-17.92, 3.57) * mm, "radius": 7 * mm});
            skSolve(sketch);
        }
        {
            var Q0;
            Q0 = qSketchRegion(id + "F5", true);
            extrude(context, id + "F6", {"entities" : qUnion([Q0]), "depth" : 25 * mm});
        }
        {
            var Q0;
            Q0=makeQuery(id+"F6.opExtrude","SWEPT_BODY",BODY,{"disambiguationData":[OSD([sQuery(id+"F5.wireOp",EDGE,"E116")])]});
            deleteBodies(context, id + "F7", {"entities" : qUnion([Q0])});
        }
    });
